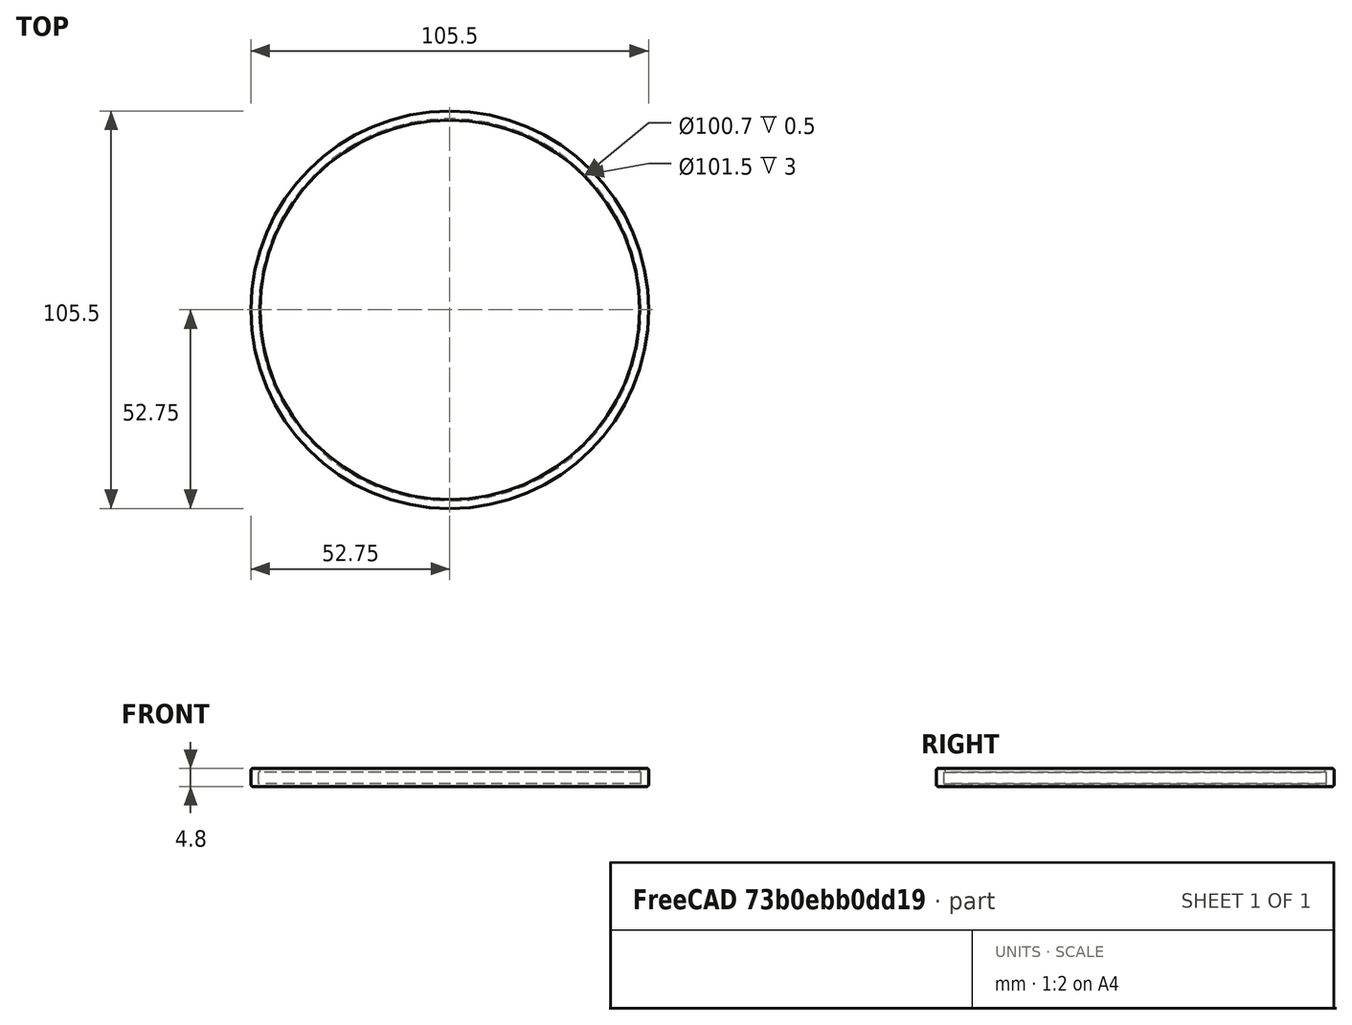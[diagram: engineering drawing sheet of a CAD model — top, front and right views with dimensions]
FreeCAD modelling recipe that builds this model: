
FCSTD DOCUMENT  (FreeCAD 1.0R38641 +678 (Git))
Label: tin_can_lid
License: All rights reserved
LicenseURL: https://en.wikipedia.org/wiki/All_rights_reserved
objects: PartDesign::Body×2, Spreadsheet::Sheet×1, Sketcher::SketchObject×1, PartDesign::Revolution×1
note: 7 computed .brp shape members not serialized (recipe doc carries the construction recipe); baked Part::Feature solids carry a one-line shape summary decoded from their .brp

FEATURE [PartDesign::Body] Body
  AllowCompound = false
  Origin = -> Origin
FEATURE [Spreadsheet::Sheet] Spreadsheet
  cells = A2='c_dia; B2(c_dia)=100.5; C2='can diameter; D2='Can lip outer diameter; A3='c_lip_h; B3(c_lip_h)=3; C3='can lip height; A4='t_dia; B4(t_dia)=0.5; C4='diameter tolerance
FEATURE [Sketcher::SketchObject] Sketch
  ArcFitTolerance = 1e-06
  AttachmentSupport = -> [XZ_Plane001]
  FullyConstrained = true
  MakeInternals = false
  MapMode = 5
  Placement = pos=(0,0,0) rot=(1,0,0;1.5708rad)
  expr: Constraints[14] = Spreadsheet.c_dia / 2 + Spreadsheet.t_dia
  expr: Constraints[16] = Spreadsheet.c_lip_h
  sketch-geometry (14):
    g0: LineSegment StartX=0 StartY=0 StartZ=0 EndX=52.25 EndY=0 EndZ=0
    g1: LineSegment StartX=0 StartY=0 StartZ=0 EndX=0 EndY=0.8 EndZ=0
    g2: LineSegment StartX=0 StartY=0.8 StartZ=0 EndX=50.75 EndY=0.8 EndZ=0
    g3: LineSegment StartX=50.75 StartY=0.8 StartZ=0 EndX=50.75 EndY=3.8 EndZ=0
    g4: LineSegment StartX=50.75 StartY=3.8 StartZ=0 EndX=50.35 EndY=3.8 EndZ=0
    g5: LineSegment StartX=50.35 StartY=3.8 StartZ=0 EndX=50.35 EndY=4.3 EndZ=0
    g6: LineSegment StartX=50.85 StartY=4.8 StartZ=0 EndX=52.25 EndY=4.8 EndZ=0
    g7: LineSegment StartX=52.75 StartY=4.3 StartZ=0 EndX=52.75 EndY=0.5 EndZ=0
    g8: ArcOfCircle CenterX=50.85 CenterY=4.3 CenterZ=0 NormalX=0 NormalY=0 NormalZ=1 AngleXU=0 Radius=0.5 StartAngle=1.5708 EndAngle=3.14159
    g9: GeomPoint [constr] X=50.35 Y=4.8 Z=0
    g10: ArcOfCircle CenterX=52.25 CenterY=4.3 CenterZ=0 NormalX=0 NormalY=0 NormalZ=1 AngleXU=0 Radius=0.5 StartAngle=0 EndAngle=1.5708
    g11: GeomPoint [constr] X=52.75 Y=4.8 Z=0
    g12: ArcOfCircle CenterX=52.25 CenterY=0.5 CenterZ=0 NormalX=0 NormalY=0 NormalZ=1 AngleXU=0 Radius=0.5 StartAngle=4.71239 EndAngle=6.28319
    g13: GeomPoint [constr] X=52.75 Y=0 Z=0
  constraints (35):
    c: Coincident(g0,g-1)
    c: PointOnObject(g13,g-1)
    c: Coincident(g1,g0)
    c: PointOnObject(g1,g-2)
    c: Coincident(g2,g1)
    c: Horizontal(g2)
    c: Coincident(g3,g2)
    c: Vertical(g3)
    c: Coincident(g4,g3)
    c: Coincident(g5,g4)
    c: Horizontal(g6)
    c: Vertical(g7)
    c: Vertical(g5)
    c: Horizontal(g4)
    c: DistanceX(g2,g2) = 50.75
    c: DistanceX(g4,g4) = 0.4
    c: DistanceY(g3,g3) = 3
    c: DistanceY(g5,g9) = 1
    c: DistanceX(g2,g11) = 2
    c: DistanceY(g13,g2) = 0.8
    c: PointOnObject(g9,g5)
    c: PointOnObject(g9,g6)
    c: Tangent(g5,g8) = 1.5708
    c: Tangent(g6,g8) = 1.5708
    c: Radius(g8) = 0.5
    c: PointOnObject(g11,g6)
    c: PointOnObject(g11,g7)
    c: Tangent(g6,g10) = 1.5708
    c: Tangent(g7,g10) = 1.5708
    c: PointOnObject(g13,g0)
    c: PointOnObject(g13,g7)
    c: Tangent(g0,g12) = -1.5708
    c: Tangent(g7,g12) = 1.5708
    c: Equal(g10,g8)
    c: Equal(g8,g12)
FEATURE [PartDesign::Revolution] Revolution
  Angle = 360
  Angle2 = 60
  Axis = (0,2e-16,1)
  Base = (0,0,0)
  Placement = pos=(0,0,0) rot=(1,0,0;1.5708rad)
  Profile = -> Sketch
  ReferenceAxis = -> Sketch [V_Axis]
  Refine = true
  Reversed = true
  Suppressed = false
  Type = 0
FEATURE [PartDesign::Body] Body001
  AllowCompound = false
  Group = -> [Sketch,Revolution]
  Origin = -> Origin001
  Tip = -> Revolution
